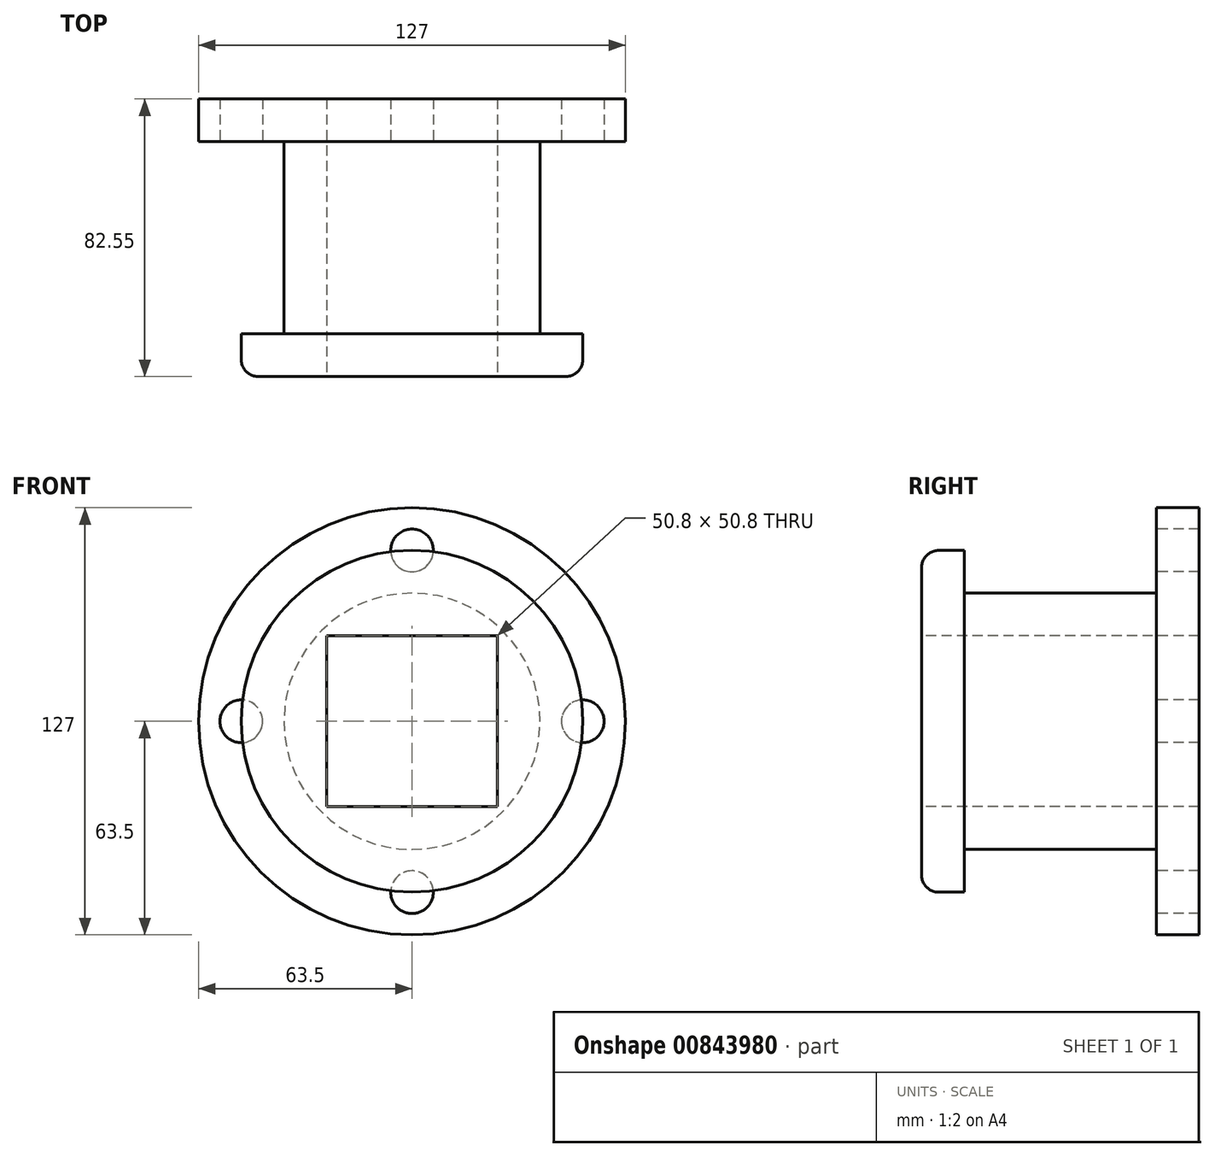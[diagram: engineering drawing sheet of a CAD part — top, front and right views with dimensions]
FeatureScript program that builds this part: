
annotation { "Feature Type Name" : "Feature", "Feature Type Description" : "" }
export const myFeature = defineFeature(function(context is Context, id is Id, definition is map)
    precondition{}
    {
        {
            var Q0;
            Q0=qCreatedBy(makeId("Front.planeOp"),FACE);
            var sketch = newSketch(context, id + "F0", { "sketchPlane" : qUnion([Q0])});
            skCircle(sketch, "E0", {"center": v(0, 0) * mm, "radius": 63.5 * mm});
            skSolve(sketch);
        }
        {
            var Q0;
            Q0=makeQuery(id+"F0.imprint","IMPRINT",FACE,{"disambiguationData":[TD([[makeQuery(id+"F0.imprint","IMPRINT",EDGE,{"derivedFrom":sQuery(id+"F0.wireOp",EDGE,"E0")}),1.0]])]});
            extrude(context, id + "F1", {"entities" : qUnion([Q0]), "depth" : 12.7 * mm, "offsetDistance" : 25.4 * mm});
        }
        {
            var Q0;
            Q0=makeQuery(id+"F1.opExtrude","CAP_FACE",FACE,{"disambiguationData":[OSD([sQuery(id+"F0.wireOp",EDGE,"E0")])],"isStart":false});
            var sketch = newSketch(context, id + "F2", { "sketchPlane" : qUnion([Q0])});
            skCircle(sketch, "E1", {"center": v(0, 0) * mm, "radius": 38.1 * mm});
            skSolve(sketch);
        }
        {
            var Q0;
            Q0=makeQuery(id+"F2.imprint","IMPRINT",FACE,{"disambiguationData":[TD([[makeQuery(id+"F2.imprint","IMPRINT",EDGE,{"derivedFrom":sQuery(id+"F2.wireOp",EDGE,"E1")}),1.0]])]});
            extrude(context, id + "F3", {"entities" : qUnion([Q0]), "operationType" : NewBodyOperationType.ADD, "depth" : 57.15 * mm, "offsetDistance" : 25.4 * mm});
        }
        {
            var Q0;
            Q0=makeQuery(id+"F3.opExtrude","CAP_FACE",FACE,{"disambiguationData":[OSD([sQuery(id+"F2.wireOp",EDGE,"E1")])],"isStart":false});
            var sketch = newSketch(context, id + "F4", { "sketchPlane" : qUnion([Q0])});
            skCircle(sketch, "E2", {"center": v(0, 0) * mm, "radius": 50.8 * mm});
            skSolve(sketch);
        }
        {
            var Q0;
            Q0=qSketchRegion(id+"F4",true);
            extrude(context, id + "F5", {"entities" : qUnion([Q0]), "operationType" : NewBodyOperationType.ADD, "depth" : 12.7 * mm, "offsetDistance" : 25.4 * mm});
        }
        {
            var Q0;
            Q0=makeQuery(id+"F1.opExtrude","CAP_FACE",FACE,{"disambiguationData":[OSD([sQuery(id+"F0.wireOp",EDGE,"E0")])],"isStart":false});
            var sketch = newSketch(context, id + "F6", { "sketchPlane" : qUnion([Q0])});
            skCircle(sketch, "E3", {"center": v(50.8, 0) * mm, "radius": 6.35 * mm});
            skCircle(sketch, "E4.1.0", {"center": v(0, 50.8) * mm, "radius": 6.35 * mm});
            skCircle(sketch, "E4.2.0", {"center": v(-50.8, 0) * mm, "radius": 6.35 * mm});
            skCircle(sketch, "E4.3.0", {"center": v(0, -50.8) * mm, "radius": 6.35 * mm});
            skPoint(sketch, "E4.center", {"position": v(0, 0) * mm});
            skSolve(sketch);
        }
        {
            var Q0;
            Q0=makeQuery(id+"F6.imprint","IMPRINT",FACE,{"disambiguationData":[TD([[makeQuery(id+"F6.imprint","IMPRINT",EDGE,{"derivedFrom":sQuery(id+"F6.wireOp",EDGE,"E3")}),1.0]])]});
            var Q1;
            Q1=makeQuery(id+"F6.imprint","IMPRINT",FACE,{"disambiguationData":[TD([[makeQuery(id+"F6.imprint","IMPRINT",EDGE,{"derivedFrom":sQuery(id+"F6.wireOp",EDGE,"E4.1.0")}),1.0]])]});
            var Q2;
            Q2=makeQuery(id+"F6.imprint","IMPRINT",FACE,{"disambiguationData":[TD([[makeQuery(id+"F6.imprint","IMPRINT",EDGE,{"derivedFrom":sQuery(id+"F6.wireOp",EDGE,"E4.2.0")}),1.0]])]});
            var Q3;
            Q3=makeQuery(id+"F6.imprint","IMPRINT",FACE,{"disambiguationData":[TD([[makeQuery(id+"F6.imprint","IMPRINT",EDGE,{"derivedFrom":sQuery(id+"F6.wireOp",EDGE,"E4.3.0")}),1.0]])]});
            extrude(context, id + "F7", {"entities" : qUnion([Q0, Q1, Q2, Q3]), "operationType" : NewBodyOperationType.REMOVE, "oppositeDirection" : true, "depth" : 25.4 * mm, "offsetDistance" : 25.4 * mm});
        }
        {
            var Q0;
            Q0=makeQuery(id+"F5.opExtrude","CAP_FACE",FACE,{"disambiguationData":[OSD([sQuery(id+"F4.wireOp",EDGE,"E2")])],"isStart":false});
            var sketch = newSketch(context, id + "F8", { "sketchPlane" : qUnion([Q0])});
            skLineSegment(sketch, "E5.bottom", {"start": v(25.4, 25.4) * mm, "end": v(-25.4, 25.4) * mm});
            skLineSegment(sketch, "E5.top", {"start": v(25.4, -25.4) * mm, "end": v(-25.4, -25.4) * mm});
            skLineSegment(sketch, "E5.left", {"start": v(25.4, 25.4) * mm, "end": v(25.4, -25.4) * mm});
            skLineSegment(sketch, "E5.right", {"start": v(-25.4, 25.4) * mm, "end": v(-25.4, -25.4) * mm});
            skPoint(sketch, "E5.middle", {"position": v(0, 0) * mm});
            skSolve(sketch);
        }
        {
            var Q0;
            Q0=qSketchRegion(id+"F8",true);
            extrude(context, id + "F9", {"entities" : qUnion([Q0]), "operationType" : NewBodyOperationType.REMOVE, "oppositeDirection" : true, "depth" : 127 * mm, "offsetDistance" : 25.4 * mm});
        }
        {
            var Q0;
            Q0=makeQuery(id+"F5.opExtrude","CAP_EDGE",EDGE,{"disambiguationData":[OSD([sQuery(id+"F4.wireOp",EDGE,"E2")])],"isStart":false});
            fillet(context, id + "F10", {"entities" : qUnion([Q0]), "radius" : 5.08 * mm, "tangentPropagation" : true, "allowEdgeOverflow" : false});
        }
    });
